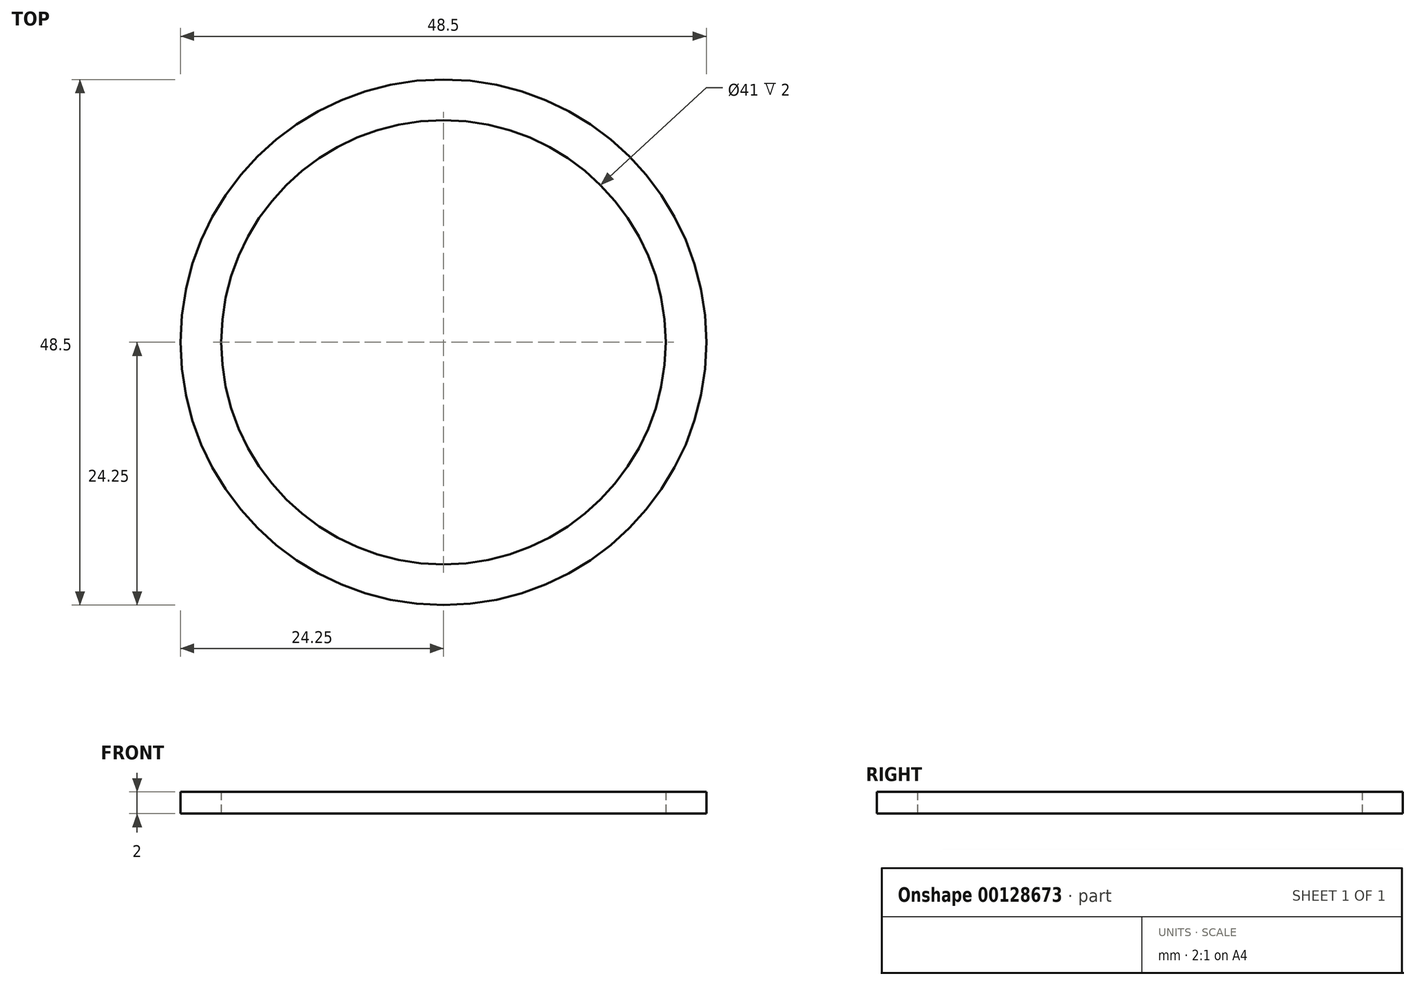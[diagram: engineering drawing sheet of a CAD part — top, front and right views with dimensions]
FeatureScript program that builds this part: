
annotation { "Feature Type Name" : "Feature", "Feature Type Description" : "" }
export const myFeature = defineFeature(function(context is Context, id is Id, definition is map)
    precondition{}
    {
        {
            var Q0;
            Q0=qCreatedBy(makeId("Top.planeOp"),FACE);
            var sketch = newSketch(context, id + "F0", { "sketchPlane" : qUnion([Q0])});
            skCircle(sketch, "E0", {"center": v(0, 0) * mm, "radius": 24.25 * mm});
            skCircle(sketch, "E1", {"center": v(0, 0) * mm, "radius": 20.5 * mm});
            skSolve(sketch);
        }
        {
            var Q0;
            Q0=makeQuery(id+"F0.imprint","IMPRINT",FACE,{"disambiguationData":[TD([[makeQuery(id+"F0.imprint","IMPRINT",EDGE,{"derivedFrom":sQuery(id+"F0.wireOp",EDGE,"E0")}),1.0]])]});
            extrude(context, id + "F1", {"entities" : qUnion([Q0]), "depth" : 2 * mm});
        }
    });
